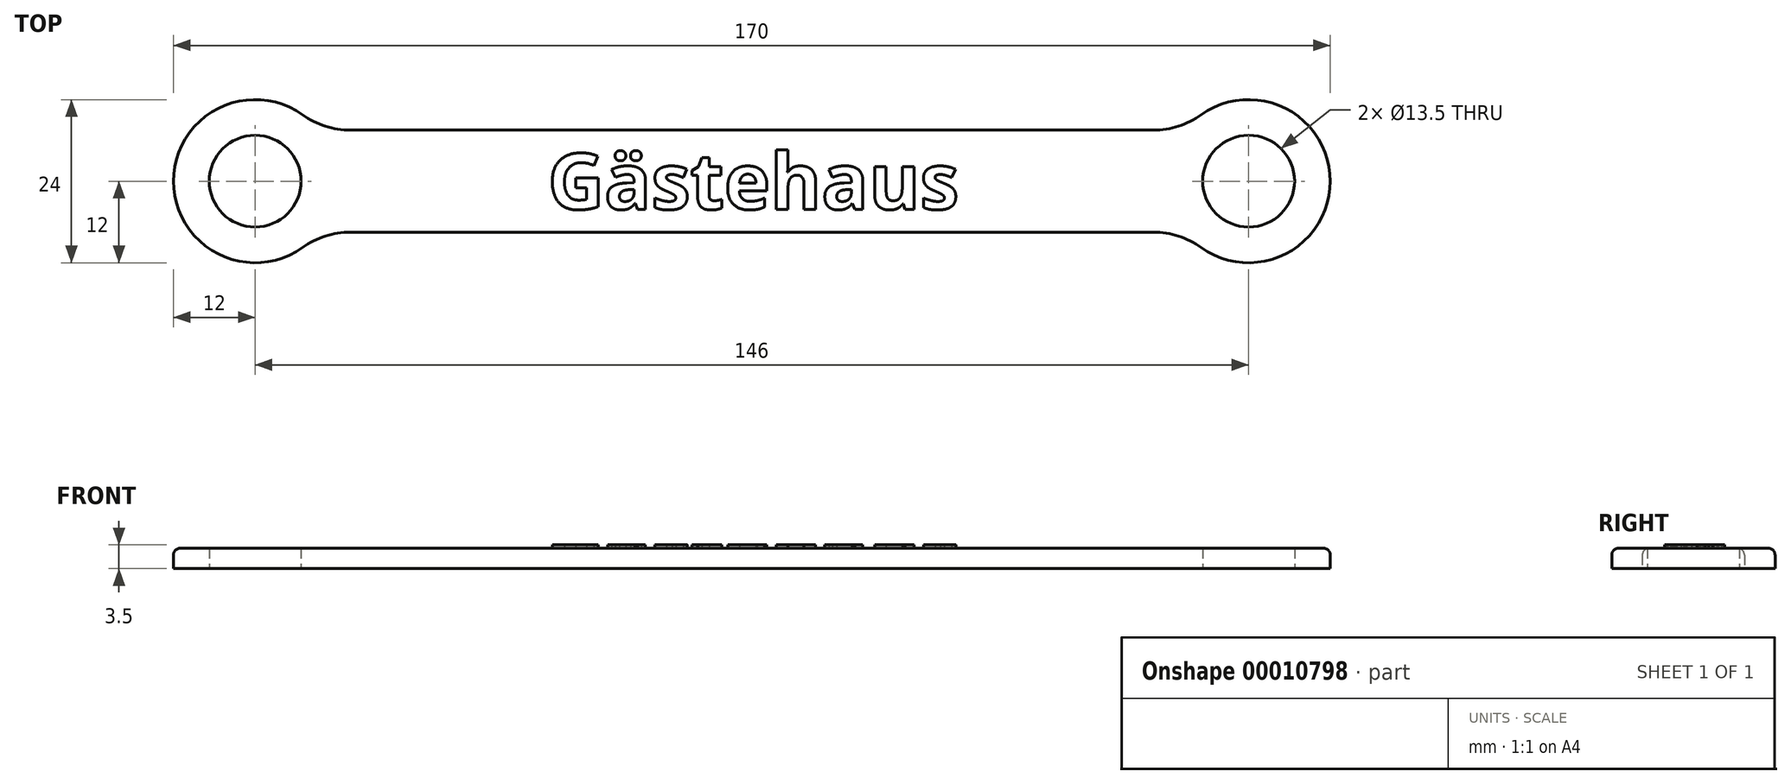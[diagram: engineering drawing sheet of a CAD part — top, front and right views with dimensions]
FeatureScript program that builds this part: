
annotation { "Feature Type Name" : "Feature", "Feature Type Description" : "" }
export const myFeature = defineFeature(function(context is Context, id is Id, definition is map)
    precondition{}
    {
        {
            var Q0;
            Q0=qCreatedBy(makeId("Top.planeOp"),FACE);
            var sketch = newSketch(context, id + "F0", { "sketchPlane" : qUnion([Q0])});
            skCircle(sketch, "E0", {"center": v(-73, 0) * mm, "radius": 6.75 * mm});
            skArc(sketch, "E1", {"start": v(-66, 9.75) * mm, "mid": v(-85, 0) * mm, "end": v(-66, -9.75) * mm});
            skLineSegment(sketch, "E2", {"start": v(0, 7.5) * mm, "end": v(-59, 7.5) * mm});
            skLineSegment(sketch, "E3", {"start": v(-59, -7.5) * mm, "end": v(0, -7.5) * mm});
            skLineSegment(sketch, "E4", {"start": v(-73, 0) * mm, "end": v(0, 0) * mm, "construction": true});
            skLineSegment(sketch, "E5", {"start": v(0, 0) * mm, "end": v(0, 32.48) * mm, "construction": true});
            skPoint(sketch, "E6.visualSharp", {"position": v(-63.63, 7.5) * mm});
            skArc(sketch, "E6.filletArc", {"start": v(-66, 9.75) * mm, "mid": v(-62.68, 8.08) * mm, "end": v(-59, 7.5) * mm});
            skPoint(sketch, "E7.visualSharp", {"position": v(-63.63, -7.5) * mm});
            skArc(sketch, "E7.filletArc", {"start": v(-59, -7.5) * mm, "mid": v(-62.68, -8.08) * mm, "end": v(-66, -9.75) * mm});
            skLineSegment(sketch, "E8.0.MirrorCS", {"start": v(0, 7.5) * mm, "end": v(59, 7.5) * mm});
            skLineSegment(sketch, "E9.0.MirrorCS", {"start": v(59, -7.5) * mm, "end": v(0, -7.5) * mm});
            skArc(sketch, "E10.0.MirrorCS", {"start": v(59, -7.5) * mm, "mid": v(62.68, -8.08) * mm, "end": v(66, -9.75) * mm});
            skArc(sketch, "E11.0.MirrorCS", {"start": v(66, 9.75) * mm, "mid": v(62.68, 8.08) * mm, "end": v(59, 7.5) * mm});
            skArc(sketch, "E12.0.MirrorCS", {"start": v(66, 9.75) * mm, "mid": v(85, 0) * mm, "end": v(66, -9.75) * mm});
            skCircle(sketch, "E13.0.MirrorC", {"center": v(73, 0) * mm, "radius": 6.75 * mm});
            skLineSegment(sketch, "E14", {"start": v(-89.97, 0) * mm, "end": v(0, 89.97) * mm, "construction": true});
            skLineSegment(sketch, "E15", {"start": v(0, 89.97) * mm, "end": v(89.97, 0) * mm, "construction": true});
            skLineSegment(sketch, "E16", {"start": v(89.97, 0) * mm, "end": v(0, -89.97) * mm, "construction": true});
            skLineSegment(sketch, "E17", {"start": v(0, -89.97) * mm, "end": v(-89.97, 0) * mm, "construction": true});
            skSolve(sketch);
        }
        {
            var Q0;
            Q0=qSketchRegion(id+"F0",true);
            extrude(context, id + "F1", {"entities" : qUnion([Q0]), "depth" : 3 * mm});
        }
        {
            var Q0;
            Q0=makeQuery(id+"F1.opExtrude","CAP_FACE",FACE,{"disambiguationData":[OSD([sQuery(id+"F0.wireOp",EDGE,"E0"),sQuery(id+"F0.wireOp",EDGE,"E1"),sQuery(id+"F0.wireOp",EDGE,"E2"),sQuery(id+"F0.wireOp",EDGE,"E3"),sQuery(id+"F0.wireOp",EDGE,"E6.filletArc"),sQuery(id+"F0.wireOp",EDGE,"E7.filletArc"),sQuery(id+"F0.wireOp",EDGE,"E8.0.MirrorCS"),sQuery(id+"F0.wireOp",EDGE,"E9.0.MirrorCS"),sQuery(id+"F0.wireOp",EDGE,"E10.0.MirrorCS"),sQuery(id+"F0.wireOp",EDGE,"E11.0.MirrorCS"),sQuery(id+"F0.wireOp",EDGE,"E12.0.MirrorCS"),sQuery(id+"F0.wireOp",EDGE,"E13.0.MirrorC")])],"isStart":false});
            var sketch = newSketch(context, id + "F2", { "sketchPlane" : qUnion([Q0])});
            skText(sketch, "E18", { "text": "Gästehaus", "fontName": "OpenSans-Bold.ttf"});
            skLineSegment(sketch, "E19", {"start": v(0, 0) * mm, "end": v(0, 25.62) * mm, "construction": true});
            skLineSegment(sketch, "E20", {"start": v(0, 0) * mm, "end": v(54.8, 0) * mm, "construction": true});
            const initialGuessF2  = {"E18": [-0.03, -0.00413, 1, 0, 0.00826]};
            skSetInitialGuess(sketch, initialGuessF2);
            skSolve(sketch);
        }
        {
            var Q0;
            Q0=qSketchRegion(id+"F2",true);
            extrude(context, id + "F3", {"entities" : qUnion([Q0]), "operationType" : NewBodyOperationType.ADD, "depth" : 0.5 * mm});
        }
        {
            var Q0;
            Q0=makeQuery(id+"F1.opExtrude","CAP_EDGE",EDGE,{"disambiguationData":[OSD([sQuery(id+"F0.wireOp",EDGE,"E3"),sQuery(id+"F0.wireOp",EDGE,"E9.0.MirrorCS")])],"isStart":false});
            fillet(context, id + "F4", {"entities" : qUnion([Q0]), "radius" : 1 * mm, "tangentPropagation" : true, "allowEdgeOverflow" : false});
        }
    });
